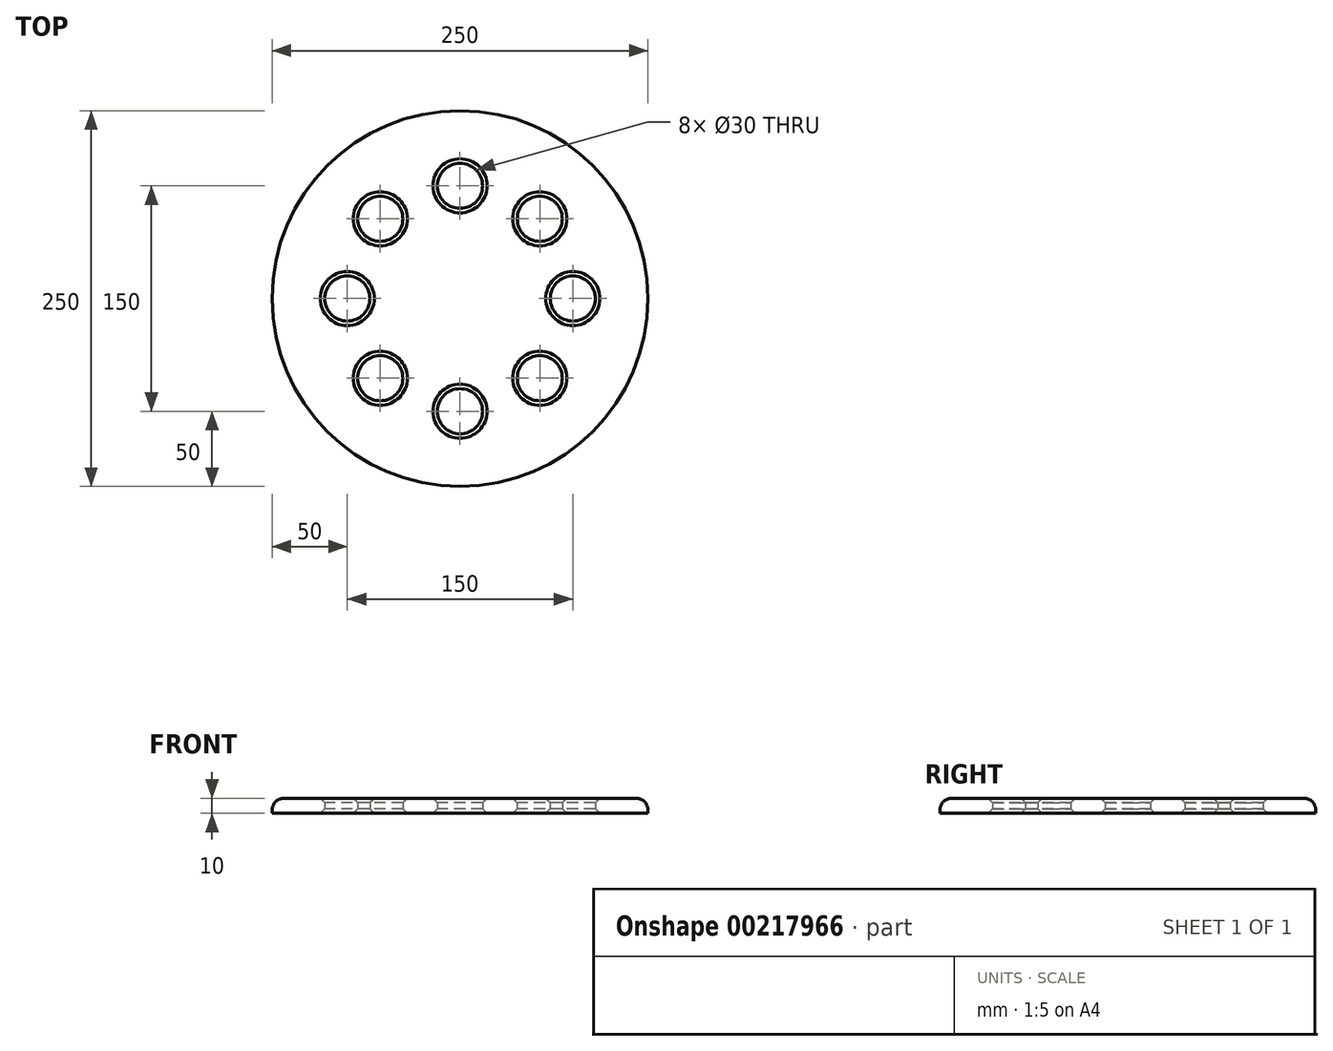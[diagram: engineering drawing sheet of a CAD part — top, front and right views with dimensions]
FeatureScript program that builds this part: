
annotation { "Feature Type Name" : "Feature", "Feature Type Description" : "" }
export const myFeature = defineFeature(function(context is Context, id is Id, definition is map)
    precondition{}
    {
        {
            var Q0;
            Q0=qCreatedBy(makeId("Top.planeOp"),FACE);
            var sketch = newSketch(context, id + "F0", { "sketchPlane" : qUnion([Q0])});
            skCircle(sketch, "E0", {"center": v(0, 0) * mm, "radius": 125 * mm});
            skSolve(sketch);
        }
        {
            var Q0;
            Q0=makeQuery(id+"F0.imprint","IMPRINT",FACE,{"disambiguationData":[TD([[makeQuery(id+"F0.imprint","IMPRINT",EDGE,{"derivedFrom":sQuery(id+"F0.wireOp",EDGE,"E0")}),1.0]])]});
            var sketch = newSketch(context, id + "F1", { "sketchPlane" : qUnion([Q0])});
            skCircle(sketch, "E1", {"center": v(0, 75) * mm, "radius": 15 * mm});
            skCircle(sketch, "E2.1.0", {"center": v(-53.03, 53.03) * mm, "radius": 15 * mm});
            skCircle(sketch, "E2.2.0", {"center": v(-75, 0) * mm, "radius": 15 * mm});
            skCircle(sketch, "E2.3.0", {"center": v(-53.03, -53.03) * mm, "radius": 15 * mm});
            skCircle(sketch, "E2.4.0", {"center": v(0, -75) * mm, "radius": 15 * mm});
            skCircle(sketch, "E2.5.0", {"center": v(53.03, -53.03) * mm, "radius": 15 * mm});
            skCircle(sketch, "E2.6.0", {"center": v(75, 0) * mm, "radius": 15 * mm});
            skCircle(sketch, "E2.7.0", {"center": v(53.03, 53.03) * mm, "radius": 15 * mm});
            skPoint(sketch, "E2.center", {"position": v(0, 0) * mm});
            skSolve(sketch);
        }
        {
            var Q0;
            Q0=makeQuery(id+"F1.imprint","IMPRINT",FACE,{"disambiguationData":[TD([[makeQuery(id+"F1.imprint","IMPRINT",EDGE,{"derivedFrom":sQuery(id+"F1.wireOp",EDGE,"E1")}),-1.0]])]});
            extrude(context, id + "F2", {"entities" : qUnion([Q0]), "depth" : 10 * mm});
        }
        {
            var Q0;
            Q0=makeQuery(id+"F2.opExtrude","CAP_EDGE",EDGE,{"disambiguationData":[OSD([sQuery(id+"F0.wireOp",EDGE,"E0")])],"isStart":false});
            fillet(context, id + "F3", {"entities" : qUnion([Q0]), "radius" : 8 * mm, "tangentPropagation" : true, "allowEdgeOverflow" : false});
        }
        {
            var Q0;
            Q0=makeQuery(id+"F2.opExtrude","CAP_EDGE",EDGE,{"disambiguationData":[OSD([sQuery(id+"F1.wireOp",EDGE,"E2.3.0")])],"isStart":false});
            var Q1;
            Q1=makeQuery(id+"F2.opExtrude","CAP_EDGE",EDGE,{"disambiguationData":[OSD([sQuery(id+"F1.wireOp",EDGE,"E2.2.0")])],"isStart":false});
            var Q2;
            Q2=makeQuery(id+"F2.opExtrude","CAP_EDGE",EDGE,{"disambiguationData":[OSD([sQuery(id+"F1.wireOp",EDGE,"E2.1.0")])],"isStart":false});
            var Q3;
            Q3=makeQuery(id+"F2.opExtrude","CAP_EDGE",EDGE,{"disambiguationData":[OSD([sQuery(id+"F1.wireOp",EDGE,"E1")])],"isStart":false});
            var Q4;
            Q4=makeQuery(id+"F2.opExtrude","CAP_EDGE",EDGE,{"disambiguationData":[OSD([sQuery(id+"F1.wireOp",EDGE,"E2.7.0")])],"isStart":false});
            var Q5;
            Q5=makeQuery(id+"F2.opExtrude","CAP_EDGE",EDGE,{"disambiguationData":[OSD([sQuery(id+"F1.wireOp",EDGE,"E2.6.0")])],"isStart":false});
            var Q6;
            Q6=makeQuery(id+"F2.opExtrude","CAP_EDGE",EDGE,{"disambiguationData":[OSD([sQuery(id+"F1.wireOp",EDGE,"E2.5.0")])],"isStart":false});
            var Q7;
            Q7=makeQuery(id+"F2.opExtrude","CAP_EDGE",EDGE,{"disambiguationData":[OSD([sQuery(id+"F1.wireOp",EDGE,"E2.4.0")])],"isStart":false});
            var Q8;
            Q8=makeQuery(id+"F2.opExtrude","CAP_EDGE",EDGE,{"disambiguationData":[OSD([sQuery(id+"F1.wireOp",EDGE,"E2.5.0")])],"isStart":true});
            var Q9;
            Q9=makeQuery(id+"F2.opExtrude","CAP_EDGE",EDGE,{"disambiguationData":[OSD([sQuery(id+"F1.wireOp",EDGE,"E2.6.0")])],"isStart":true});
            var Q10;
            Q10=makeQuery(id+"F2.opExtrude","CAP_EDGE",EDGE,{"disambiguationData":[OSD([sQuery(id+"F1.wireOp",EDGE,"E2.7.0")])],"isStart":true});
            var Q11;
            Q11=makeQuery(id+"F2.opExtrude","CAP_EDGE",EDGE,{"disambiguationData":[OSD([sQuery(id+"F1.wireOp",EDGE,"E1")])],"isStart":true});
            var Q12;
            Q12=makeQuery(id+"F2.opExtrude","CAP_EDGE",EDGE,{"disambiguationData":[OSD([sQuery(id+"F1.wireOp",EDGE,"E2.1.0")])],"isStart":true});
            var Q13;
            Q13=makeQuery(id+"F2.opExtrude","CAP_EDGE",EDGE,{"disambiguationData":[OSD([sQuery(id+"F1.wireOp",EDGE,"E2.2.0")])],"isStart":true});
            var Q14;
            Q14=makeQuery(id+"F2.opExtrude","CAP_EDGE",EDGE,{"disambiguationData":[OSD([sQuery(id+"F1.wireOp",EDGE,"E2.3.0")])],"isStart":true});
            var Q15;
            Q15=makeQuery(id+"F2.opExtrude","CAP_EDGE",EDGE,{"disambiguationData":[OSD([sQuery(id+"F1.wireOp",EDGE,"E2.4.0")])],"isStart":true});
            chamfer(context, id + "F4", {"entities" : qUnion([Q0, Q1, Q2, Q3, Q4, Q5, Q6, Q7, Q8, Q9, Q10, Q11, Q12, Q13, Q14, Q15]), "width" : 3 * mm, "tangentPropagation" : true});
        }
    });
